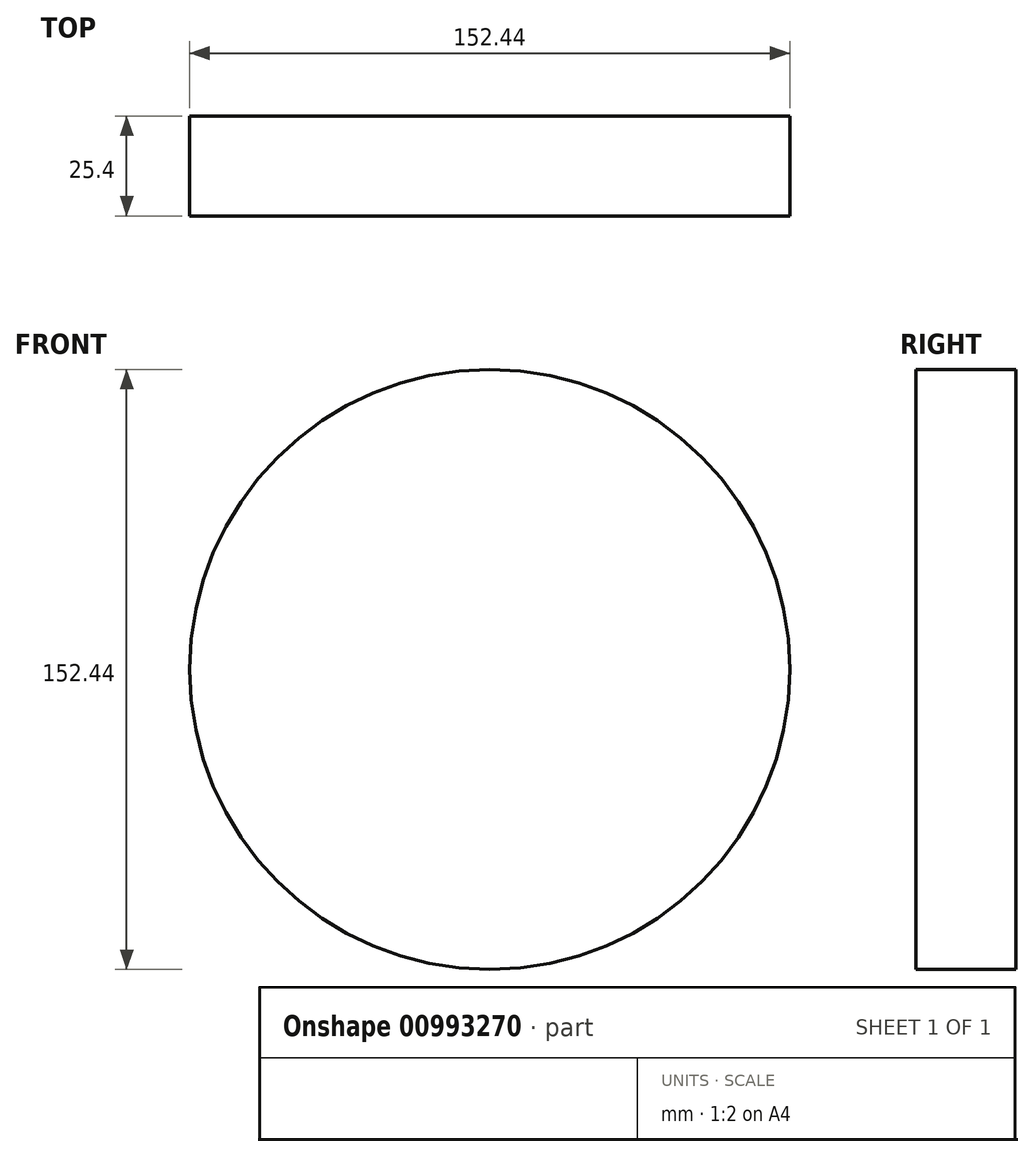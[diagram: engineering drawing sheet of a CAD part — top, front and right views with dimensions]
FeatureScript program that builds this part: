
annotation { "Feature Type Name" : "Feature", "Feature Type Description" : "" }
export const myFeature = defineFeature(function(context is Context, id is Id, definition is map)
    precondition{}
    {
        {
            var Q0;
            Q0=qCreatedBy(makeId("Front.planeOp"),FACE);
            var sketch = newSketch(context, id + "F0", { "sketchPlane" : qUnion([Q0])});
            skCircle(sketch, "E0", {"center": v(0, 0) * mm, "radius": 76.22 * mm});
            skSolve(sketch);
        }
        {
            var Q0;
            Q0=makeQuery(id+"F0.imprint","IMPRINT",FACE,{"disambiguationData":[TD([[makeQuery(id+"F0.imprint","IMPRINT",EDGE,{"derivedFrom":sQuery(id+"F0.wireOp",EDGE,"E0")}),1.0]])]});
            extrude(context, id + "F1", {"entities" : qUnion([Q0]), "depth" : 25.4 * mm, "offsetDistance" : 25.4 * mm});
        }
    });
